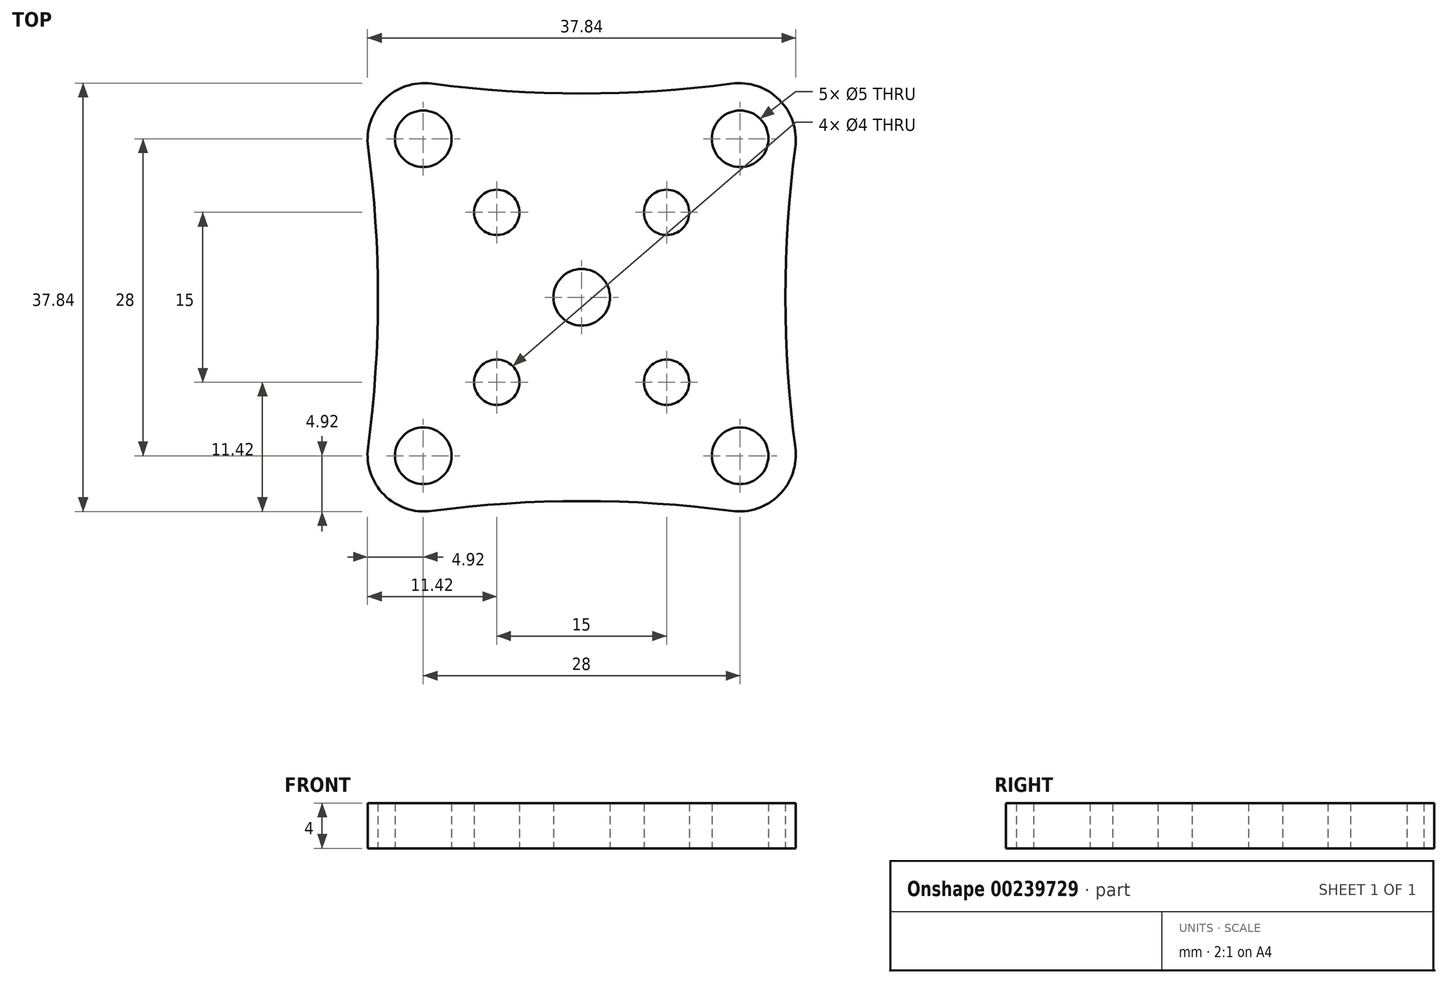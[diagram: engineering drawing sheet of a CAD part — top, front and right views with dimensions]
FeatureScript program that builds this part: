
annotation { "Feature Type Name" : "Feature", "Feature Type Description" : "" }
export const myFeature = defineFeature(function(context is Context, id is Id, definition is map)
    precondition{}
    {
        {
            var Q0;
            Q0=qCreatedBy(makeId("Top.planeOp"),FACE);
            var sketch = newSketch(context, id + "F0", { "sketchPlane" : qUnion([Q0])});
            skLineSegment(sketch, "E0.bottom", {"start": v(7.5, -7.5) * mm, "end": v(-7.5, -7.5) * mm});
            skLineSegment(sketch, "E0.top", {"start": v(7.5, 7.5) * mm, "end": v(-7.5, 7.5) * mm});
            skLineSegment(sketch, "E0.left", {"start": v(7.5, -7.5) * mm, "end": v(7.5, 7.5) * mm});
            skLineSegment(sketch, "E0.right", {"start": v(-7.5, -7.5) * mm, "end": v(-7.5, 7.5) * mm});
            skPoint(sketch, "E0.middle", {"position": v(0, 0) * mm});
            skCircle(sketch, "E1", {"center": v(-7.5, 7.5) * mm, "radius": 5 * mm});
            skCircle(sketch, "E2", {"center": v(7.5, 7.5) * mm, "radius": 5 * mm});
            skCircle(sketch, "E3", {"center": v(-7.5, -7.5) * mm, "radius": 5 * mm});
            skCircle(sketch, "E4", {"center": v(7.5, -7.5) * mm, "radius": 5 * mm});
            skCircle(sketch, "E5", {"center": v(-7.5, 7.5) * mm, "radius": 2 * mm});
            skCircle(sketch, "E6", {"center": v(7.5, 7.5) * mm, "radius": 2 * mm});
            skCircle(sketch, "E7", {"center": v(7.5, -7.5) * mm, "radius": 2 * mm});
            skCircle(sketch, "E8", {"center": v(-7.5, -7.5) * mm, "radius": 2 * mm});
            skCircle(sketch, "E9", {"center": v(0, 0) * mm, "radius": 2.5 * mm});
            skLineSegment(sketch, "E10.bottom", {"start": v(20, -20) * mm, "end": v(-20, -20) * mm});
            skLineSegment(sketch, "E10.top", {"start": v(20, 20) * mm, "end": v(-20, 20) * mm});
            skLineSegment(sketch, "E10.left", {"start": v(20, -20) * mm, "end": v(20, 20) * mm});
            skLineSegment(sketch, "E10.right", {"start": v(-20, -20) * mm, "end": v(-20, 20) * mm});
            skPoint(sketch, "E11.centerSnap0", {"position": v(0, -20) * mm});
            skCircle(sketch, "E12.cCircle", {"center": v(0, 0) * mm, "radius": 14 * mm, "construction": true});
            skLineSegment(sketch, "E12.0", {"start": v(14, 14) * mm, "end": v(14, -14) * mm});
            skLineSegment(sketch, "E12.1", {"start": v(14, -14) * mm, "end": v(-14, -14) * mm});
            skLineSegment(sketch, "E12.2", {"start": v(-14, -14) * mm, "end": v(-14, 14) * mm});
            skLineSegment(sketch, "E12.3", {"start": v(-14, 14) * mm, "end": v(14, 14) * mm});
            skPoint(sketch, "E12.0.midPoint", {"position": v(14, 0) * mm});
            skCircle(sketch, "E13", {"center": v(14, 14) * mm, "radius": 2.5 * mm});
            skCircle(sketch, "E14", {"center": v(-14, -14) * mm, "radius": 2.5 * mm});
            skCircle(sketch, "E15", {"center": v(14, -14) * mm, "radius": 2.5 * mm});
            skCircle(sketch, "E16", {"center": v(-14, 14) * mm, "radius": 2.5 * mm});
            skArc(sketch, "E17", {"start": v(-20, 20) * mm, "mid": v(0, 18) * mm, "end": v(20, 20) * mm});
            skArc(sketch, "E18", {"start": v(20, 20) * mm, "mid": v(18, 0) * mm, "end": v(20, -20) * mm});
            skArc(sketch, "E19", {"start": v(20, -20) * mm, "mid": v(0, -18) * mm, "end": v(-20, -20) * mm});
            skArc(sketch, "E20", {"start": v(-20, -20) * mm, "mid": v(-18, 0) * mm, "end": v(-20, 20) * mm});
            skSolve(sketch);
        }
        {
            var Q0;
            Q0=makeQuery(id+"F0.imprint","IMPRINT",FACE,{"disambiguationData":[TD([[makeQuery(id+"F0.imprint","IMPRINT",EDGE,{"derivedFrom":sQuery(id+"F0.wireOp",EDGE,"E17")}),-1.0]])]});
            var Q1;
            {var subQ5=sQuery(id+"F0.wireOp",EDGE,"E4");var subQ6=sQuery(id+"F0.wireOp",EDGE,"E0.bottom");var subQ7=makeQuery(id+"F0.imprint","INTERSECT",VERTEX,{"derivedFrom":[subQ6,subQ5]});Q1=makeQuery(id+"F0.imprint","IMPRINT",FACE,{"disambiguationData":[TD([[makeQuery(id+"F0.imprint","IMPRINT",EDGE,{"disambiguationData":[TD([[subQ7,-1.0]])],"derivedFrom":subQ6}),1.0]])]});}
            var Q2;
            Q2=makeQuery(id+"F0.imprint","IMPRINT",FACE,{"disambiguationData":[TD([[makeQuery(id+"F0.imprint","IMPRINT",EDGE,{"derivedFrom":sQuery(id+"F0.wireOp",EDGE,"E9")}),-1.0]])]});
            var Q3;
            {var subQ0=sQuery(id+"F0.wireOp",EDGE,"E1");var subQ1=sQuery(id+"F0.wireOp",EDGE,"E0.top");var subQ2=makeQuery(id+"F0.imprint","INTERSECT",VERTEX,{"derivedFrom":[subQ1,subQ0]});Q3=makeQuery(id+"F0.imprint","IMPRINT",FACE,{"disambiguationData":[TD([[makeQuery(id+"F0.imprint","IMPRINT",EDGE,{"disambiguationData":[TD([[subQ2,-1.0]])],"derivedFrom":subQ1}),1.0]])]});}
            var Q4;
            {var subQ0=sQuery(id+"F0.wireOp",EDGE,"E1");var subQ1=sQuery(id+"F0.wireOp",EDGE,"E0.top");var subQ2=makeQuery(id+"F0.imprint","INTERSECT",VERTEX,{"derivedFrom":[subQ1,subQ0]});Q4=makeQuery(id+"F0.imprint","IMPRINT",FACE,{"disambiguationData":[TD([[makeQuery(id+"F0.imprint","IMPRINT",EDGE,{"disambiguationData":[TD([[subQ2,-1.0]])],"derivedFrom":subQ1}),-1.0]])]});}
            var Q5;
            {var subQ0=sQuery(id+"F0.wireOp",EDGE,"E6");var subQ1=sQuery(id+"F0.wireOp",EDGE,"E0.top");var subQ2=makeQuery(id+"F0.imprint","INTERSECT",VERTEX,{"derivedFrom":[subQ1,subQ0]});Q5=makeQuery(id+"F0.imprint","IMPRINT",FACE,{"disambiguationData":[TD([[makeQuery(id+"F0.imprint","IMPRINT",EDGE,{"disambiguationData":[TD([[subQ2,-1.0]])],"derivedFrom":subQ1}),-1.0]])]});}
            var Q6;
            {var subQ0=sQuery(id+"F0.wireOp",EDGE,"E6");var subQ1=sQuery(id+"F0.wireOp",EDGE,"E0.top");var subQ2=makeQuery(id+"F0.imprint","INTERSECT",VERTEX,{"derivedFrom":[subQ1,subQ0]});Q6=makeQuery(id+"F0.imprint","IMPRINT",FACE,{"disambiguationData":[TD([[makeQuery(id+"F0.imprint","IMPRINT",EDGE,{"disambiguationData":[TD([[subQ2,-1.0]])],"derivedFrom":subQ1}),1.0]])]});}
            var Q7;
            {var subQ0=sQuery(id+"F0.wireOp",EDGE,"E3");var subQ1=sQuery(id+"F0.wireOp",EDGE,"E0.bottom");var subQ2=makeQuery(id+"F0.imprint","INTERSECT",VERTEX,{"derivedFrom":[subQ1,subQ0]});Q7=makeQuery(id+"F0.imprint","IMPRINT",FACE,{"disambiguationData":[TD([[makeQuery(id+"F0.imprint","IMPRINT",EDGE,{"disambiguationData":[TD([[subQ2,-1.0]])],"derivedFrom":subQ1}),1.0]])]});}
            var Q8;
            {var subQ0=sQuery(id+"F0.wireOp",EDGE,"E7");var subQ1=sQuery(id+"F0.wireOp",EDGE,"E0.bottom");var subQ2=makeQuery(id+"F0.imprint","INTERSECT",VERTEX,{"derivedFrom":[subQ1,subQ0]});Q8=makeQuery(id+"F0.imprint","IMPRINT",FACE,{"disambiguationData":[TD([[makeQuery(id+"F0.imprint","IMPRINT",EDGE,{"disambiguationData":[TD([[subQ2,-1.0]])],"derivedFrom":subQ1}),1.0]])]});}
            var Q9;
            {var subQ0=sQuery(id+"F0.wireOp",EDGE,"E7");var subQ1=sQuery(id+"F0.wireOp",EDGE,"E0.bottom");var subQ2=makeQuery(id+"F0.imprint","INTERSECT",VERTEX,{"derivedFrom":[subQ1,subQ0]});Q9=makeQuery(id+"F0.imprint","IMPRINT",FACE,{"disambiguationData":[TD([[makeQuery(id+"F0.imprint","IMPRINT",EDGE,{"disambiguationData":[TD([[subQ2,-1.0]])],"derivedFrom":subQ1}),-1.0]])]});}
            var Q10;
            {var subQ0=sQuery(id+"F0.wireOp",EDGE,"E3");var subQ1=sQuery(id+"F0.wireOp",EDGE,"E0.bottom");var subQ2=makeQuery(id+"F0.imprint","INTERSECT",VERTEX,{"derivedFrom":[subQ1,subQ0]});Q10=makeQuery(id+"F0.imprint","IMPRINT",FACE,{"disambiguationData":[TD([[makeQuery(id+"F0.imprint","IMPRINT",EDGE,{"disambiguationData":[TD([[subQ2,-1.0]])],"derivedFrom":subQ1}),-1.0]])]});}
            extrude(context, id + "F1", {"entities" : qUnion([Q0, Q1, Q2, Q3, Q4, Q5, Q6, Q7, Q8, Q9, Q10]), "depth" : 4 * mm});
        }
        {
            var Q0;
            Q0=makeQuery(id+"F1.opExtrude","SWEPT_EDGE",EDGE,{"disambiguationData":[OSD([sQuery(id+"F0.wireOp",EDGE,"E10.bottom"),sQuery(id+"F0.wireOp",EDGE,"E10.left"),sQuery(id+"F0.wireOp",EDGE,"E18"),sQuery(id+"F0.wireOp",EDGE,"E19")])]});
            var Q1;
            Q1=makeQuery(id+"F1.opExtrude","SWEPT_EDGE",EDGE,{"disambiguationData":[OSD([sQuery(id+"F0.wireOp",EDGE,"E10.top"),sQuery(id+"F0.wireOp",EDGE,"E10.left"),sQuery(id+"F0.wireOp",EDGE,"E17"),sQuery(id+"F0.wireOp",EDGE,"E18")])]});
            var Q2;
            Q2=makeQuery(id+"F1.opExtrude","SWEPT_EDGE",EDGE,{"disambiguationData":[OSD([sQuery(id+"F0.wireOp",EDGE,"E10.bottom"),sQuery(id+"F0.wireOp",EDGE,"E10.right"),sQuery(id+"F0.wireOp",EDGE,"E19"),sQuery(id+"F0.wireOp",EDGE,"E20")])]});
            var Q3;
            Q3=makeQuery(id+"F1.opExtrude","SWEPT_EDGE",EDGE,{"disambiguationData":[OSD([sQuery(id+"F0.wireOp",EDGE,"E10.top"),sQuery(id+"F0.wireOp",EDGE,"E10.right"),sQuery(id+"F0.wireOp",EDGE,"E17"),sQuery(id+"F0.wireOp",EDGE,"E20")])]});
            fillet(context, id + "F2", {"entities" : qUnion([Q0, Q1, Q2, Q3]), "radius" : 5 * mm, "tangentPropagation" : true, "allowEdgeOverflow" : false});
        }
    });
